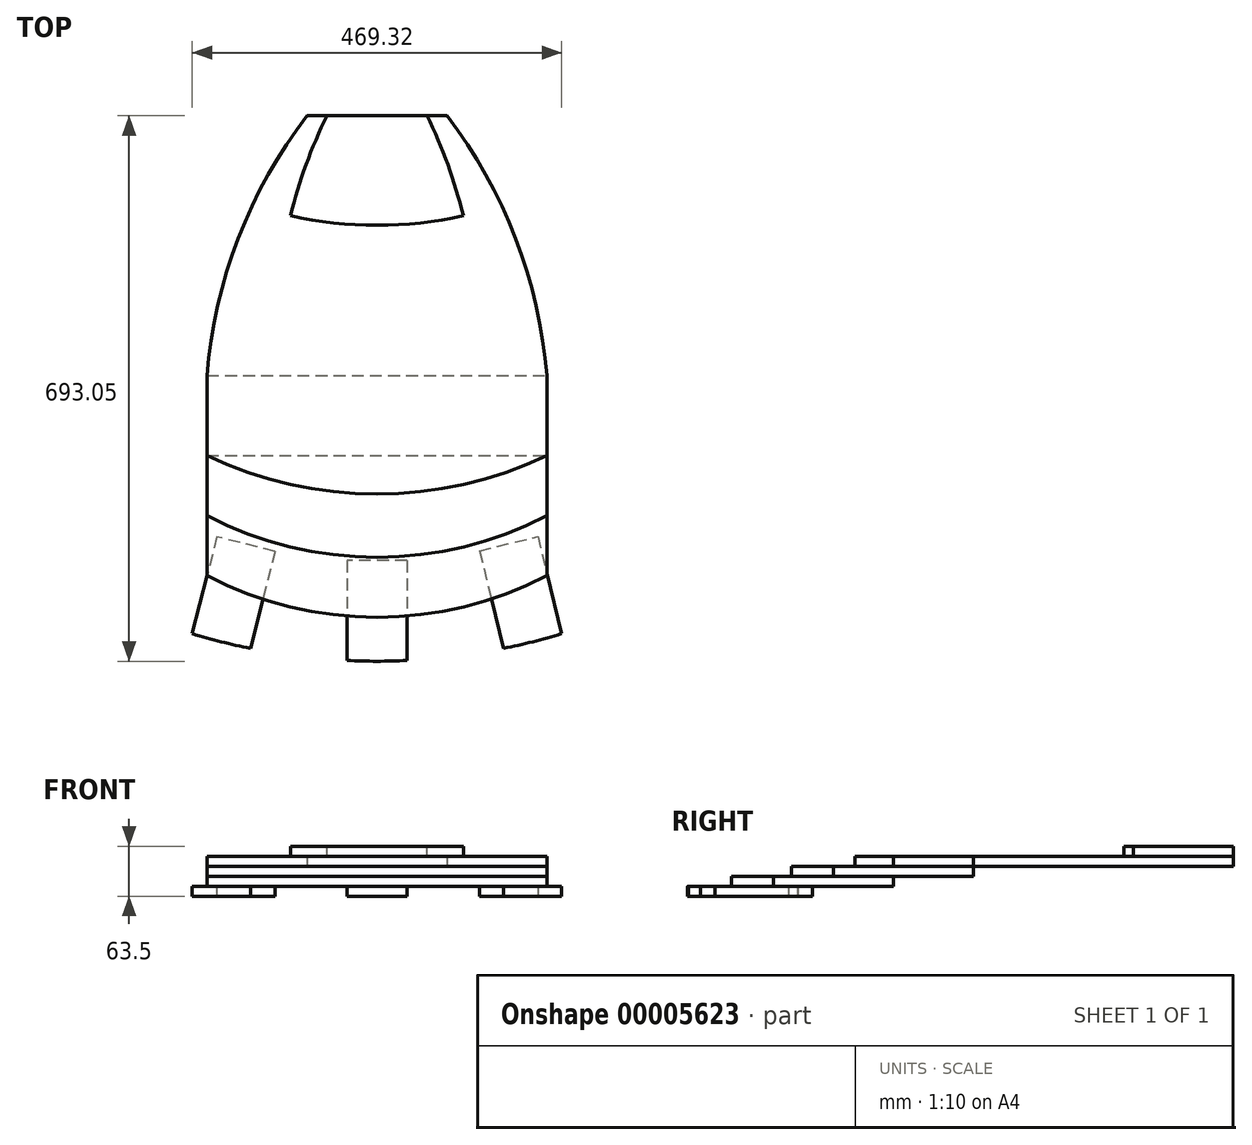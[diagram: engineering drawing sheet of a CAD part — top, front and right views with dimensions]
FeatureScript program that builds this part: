
annotation { "Feature Type Name" : "Feature", "Feature Type Description" : "" }
export const myFeature = defineFeature(function(context is Context, id is Id, definition is map)
    precondition{}
    {
        {
            var Q0;
            Q0=qCreatedBy(makeId("Top.planeOp"),FACE);
            cPlane(context, id + "F0", {"entities" : qUnion([Q0]), "cplaneType" : CPlaneType.OFFSET, "offset" : 25.4 * mm, "oppositeDirection" : true, "width" : 152.4 * mm, "height" : 152.4 * mm});
        }
        {
            var Q0;
            Q0=qCreatedBy(makeId("Top.planeOp"),FACE);
            cPlane(context, id + "F1", {"entities" : qUnion([Q0]), "cplaneType" : CPlaneType.OFFSET, "offset" : 38.1 * mm, "oppositeDirection" : true, "width" : 152.4 * mm, "height" : 152.4 * mm});
        }
        {
            var Q0;
            Q0=qCreatedBy(makeId("Top.planeOp"),FACE);
            cPlane(context, id + "F2", {"entities" : qUnion([Q0]), "cplaneType" : CPlaneType.OFFSET, "offset" : 50.8 * mm, "oppositeDirection" : true, "width" : 152.4 * mm, "height" : 152.4 * mm});
        }
        {
            var Q0;
            Q0=qCreatedBy(makeId("Top.planeOp"),FACE);
            cPlane(context, id + "F3", {"entities" : qUnion([Q0]), "cplaneType" : CPlaneType.OFFSET, "offset" : 63.5 * mm, "oppositeDirection" : true, "width" : 152.4 * mm, "height" : 152.4 * mm});
        }
        {
            var Q0;
            Q0=qCreatedBy(makeId("Top.planeOp"),FACE);
            var sketch = newSketch(context, id + "F4", { "sketchPlane" : qUnion([Q0])});
            skLineSegment(sketch, "E0.bottom", {"start": v(63.5, 0) * mm, "end": v(-63.5, 0) * mm});
            skArc(sketch, "E1.0.MirrorCS", {"start": v(-109.72, -127) * mm, "mid": v(-90.04, -62.25) * mm, "end": v(-63.5, 0) * mm});
            skArc(sketch, "E2.0.MirrorCS", {"start": v(109.72, -127) * mm, "mid": v(0, -139.15) * mm, "end": v(-109.72, -127) * mm});
            skArc(sketch, "E3.0.MirrorCS", {"start": v(63.5, 0) * mm, "mid": v(90.04, -62.25) * mm, "end": v(109.72, -127) * mm});
            skSolve(sketch);
        }
        {
            var Q0;
            Q0=makeQuery(id+"F4.imprint","IMPRINT",FACE,{"disambiguationData":[TD([[makeQuery(id+"F4.imprint","IMPRINT",EDGE,{"derivedFrom":sQuery(id+"F4.wireOp",EDGE,"E0.bottom")}),1.0]])]});
            extrude(context, id + "F5", {"entities" : qUnion([Q0]), "oppositeDirection" : true, "depth" : 12.7 * mm});
        }
        {
            var Q0;
            Q0=qCreatedBy(id+"F0.planeOp",FACE);
            var sketch = newSketch(context, id + "F6", { "sketchPlane" : qUnion([Q0])});
            skLineSegment(sketch, "E4", {"start": v(-88.9, 0) * mm, "end": v(88.9, 0) * mm});
            skArc(sketch, "E5", {"start": v(-215.9, -431.8) * mm, "mid": v(0, -480.67) * mm, "end": v(215.9, -431.8) * mm});
            skArc(sketch, "E6", {"start": v(-88.9, 0) * mm, "mid": v(-176.18, -155.96) * mm, "end": v(-215.9, -330.2) * mm});
            skArc(sketch, "E7", {"start": v(215.9, -330.2) * mm, "mid": v(176.18, -155.96) * mm, "end": v(88.9, 0) * mm});
            skLineSegment(sketch, "E8", {"start": v(-215.9, -431.8) * mm, "end": v(-215.9, -330.2) * mm});
            skLineSegment(sketch, "E9", {"start": v(215.9, -431.8) * mm, "end": v(215.9, -330.2) * mm});
            skSolve(sketch);
        }
        {
            var Q0;
            Q0=makeQuery(id+"F6.imprint","IMPRINT",FACE,{"disambiguationData":[TD([[makeQuery(id+"F6.imprint","IMPRINT",EDGE,{"derivedFrom":makeQuery(id+"F5.opExtrude","CAP_EDGE",EDGE,{"disambiguationData":[OSD([sQuery(id+"F4.wireOp",EDGE,"E0.top")])],"isStart":false})}),-1.0]])]});
            var Q1;
            Q1=makeQuery(id+"F6.imprint","IMPRINT",FACE,{"disambiguationData":[TD([[makeQuery(id+"F6.imprint","IMPRINT",EDGE,{"derivedFrom":sQuery(id+"F6.wireOp",EDGE,"E5")}),1.0]])]});
            var Q2;
            {var subQ1=makeQuery(id+"F5.opExtrude","CAP_EDGE",EDGE,{"disambiguationData":[OSD([sQuery(id+"F4.wireOp",EDGE,"8de56a55-3745-45d6-922e-69d785513ef6")])],"isStart":false});Q2=makeQuery(id+"F6.imprint","IMPRINT",FACE,{"disambiguationData":[TD([[makeQuery(id+"F6.imprint","IMPRINT",EDGE,{"derivedFrom":subQ1}),-1.0]])]});}
            extrude(context, id + "F7", {"entities" : qUnion([Q0, Q1, Q2]), "depth" : 12.7 * mm});
        }
        {
            var Q0;
            Q0=qCreatedBy(id+"F1.planeOp",FACE);
            var sketch = newSketch(context, id + "F8", { "sketchPlane" : qUnion([Q0])});
            skLineSegment(sketch, "E10", {"start": v(-215.9, -330.2) * mm, "end": v(215.9, -330.2) * mm});
            skLineSegment(sketch, "E11", {"start": v(215.9, -330.2) * mm, "end": v(215.9, -508) * mm});
            skLineSegment(sketch, "E12", {"start": v(-215.9, -508) * mm, "end": v(-215.9, -330.2) * mm});
            skArc(sketch, "E13", {"start": v(-215.9, -508) * mm, "mid": v(0, -561) * mm, "end": v(215.9, -508) * mm});
            skSolve(sketch);
        }
        {
            var Q0;
            {var subQ3=sQuery(id+"F8.wireOp",EDGE,"E10");Q0=makeQuery(id+"F8.imprint","IMPRINT",FACE,{"disambiguationData":[TD([[makeQuery(id+"F8.imprint","IMPRINT",EDGE,{"derivedFrom":subQ3}),-1.0]])]});}
            var Q1;
            {var subQ1=sQuery(id+"F8.wireOp",EDGE,"E13");Q1=makeQuery(id+"F8.imprint","IMPRINT",FACE,{"disambiguationData":[TD([[makeQuery(id+"F8.imprint","IMPRINT",EDGE,{"derivedFrom":subQ1}),1.0]])]});}
            extrude(context, id + "F9", {"entities" : qUnion([Q0, Q1]), "depth" : 12.7 * mm});
        }
        {
            var Q0;
            Q0=qCreatedBy(id+"F2.planeOp",FACE);
            var sketch = newSketch(context, id + "F10", { "sketchPlane" : qUnion([Q0])});
            skLineSegment(sketch, "E14", {"start": v(-215.9, -431.8) * mm, "end": v(215.9, -431.8) * mm});
            skLineSegment(sketch, "E15", {"start": v(215.9, -431.8) * mm, "end": v(215.9, -584.2) * mm});
            skLineSegment(sketch, "E16", {"start": v(-215.9, -584.2) * mm, "end": v(-215.9, -431.8) * mm});
            skArc(sketch, "E17", {"start": v(-215.9, -584.2) * mm, "mid": v(0, -637.2) * mm, "end": v(215.9, -584.2) * mm});
            skSolve(sketch);
        }
        {
            var Q0;
            {var subQ3=sQuery(id+"F10.wireOp",EDGE,"E14");Q0=makeQuery(id+"F10.imprint","IMPRINT",FACE,{"disambiguationData":[TD([[makeQuery(id+"F10.imprint","IMPRINT",EDGE,{"derivedFrom":subQ3}),-1.0]])]});}
            var Q1;
            {var subQ1=sQuery(id+"F10.wireOp",EDGE,"E17");Q1=makeQuery(id+"F10.imprint","IMPRINT",FACE,{"disambiguationData":[TD([[makeQuery(id+"F10.imprint","IMPRINT",EDGE,{"derivedFrom":subQ1}),1.0]])]});}
            extrude(context, id + "F11", {"entities" : qUnion([Q0, Q1]), "depth" : 12.7 * mm});
        }
        {
            var Q0;
            Q0=qCreatedBy(id+"F3.planeOp",FACE);
            var sketch = newSketch(context, id + "F12", { "sketchPlane" : qUnion([Q0])});
            skLineSegment(sketch, "E18.bottom", {"start": v(130.48, -552.79) * mm, "end": v(204.5, -534.69) * mm});
            skLineSegment(sketch, "E18.left", {"start": v(130.48, -552.79) * mm, "end": v(160.8, -676.81) * mm});
            skLineSegment(sketch, "E18.right", {"start": v(204.5, -534.69) * mm, "end": v(234.66, -658.06) * mm});
            skLineSegment(sketch, "E19.bottom", {"start": v(-129.54, -553.72) * mm, "end": v(-203.4, -534.96) * mm});
            skLineSegment(sketch, "E19.left", {"start": v(-129.54, -553.72) * mm, "end": v(-160.8, -676.81) * mm});
            skLineSegment(sketch, "E19.right", {"start": v(-203.4, -534.96) * mm, "end": v(-234.66, -658.06) * mm});
            skLineSegment(sketch, "E20.bottom", {"start": v(38.1, -565.15) * mm, "end": v(-38.1, -565.15) * mm});
            skLineSegment(sketch, "E20.left", {"start": v(38.1, -565.15) * mm, "end": v(38.1, -692.15) * mm});
            skLineSegment(sketch, "E20.right", {"start": v(-38.1, -565.15) * mm, "end": v(-38.1, -692.15) * mm});
            skArc(sketch, "E21", {"start": v(-234.66, -658.06) * mm, "mid": v(-197.95, -668.3) * mm, "end": v(-160.8, -676.81) * mm});
            skArc(sketch, "E22.trimOffspring", {"start": v(160.8, -676.81) * mm, "mid": v(197.95, -668.3) * mm, "end": v(234.66, -658.06) * mm});
            skArc(sketch, "E23.trimOffspring", {"start": v(-38.1, -692.15) * mm, "mid": v(0, -693.05) * mm, "end": v(38.1, -692.15) * mm});
            skSolve(sketch);
        }
        {
            var Q0;
            {var subQ5=sQuery(id+"F12.wireOp",EDGE,"E18.bottom");Q0=makeQuery(id+"F12.imprint","IMPRINT",FACE,{"disambiguationData":[TD([[makeQuery(id+"F12.imprint","IMPRINT",EDGE,{"derivedFrom":subQ5}),-1.0]])]});}
            var Q1;
            {var subQ7=sQuery(id+"F12.wireOp",EDGE,"E22.trimOffspring");Q1=makeQuery(id+"F12.imprint","IMPRINT",FACE,{"disambiguationData":[TD([[makeQuery(id+"F12.imprint","IMPRINT",EDGE,{"derivedFrom":subQ7}),1.0]])]});}
            extrude(context, id + "F13", {"entities" : qUnion([Q0, Q1]), "operationType" : NewBodyOperationType.ADD, "depth" : 12.7 * mm});
        }
        {
            var Q0;
            {var subQ5=sQuery(id+"F12.wireOp",EDGE,"E20.bottom");Q0=makeQuery(id+"F12.imprint","IMPRINT",FACE,{"disambiguationData":[TD([[makeQuery(id+"F12.imprint","IMPRINT",EDGE,{"derivedFrom":subQ5}),1.0]])]});}
            var Q1;
            {var subQ5=sQuery(id+"F12.wireOp",EDGE,"E23.trimOffspring");Q1=makeQuery(id+"F12.imprint","IMPRINT",FACE,{"disambiguationData":[TD([[makeQuery(id+"F12.imprint","IMPRINT",EDGE,{"derivedFrom":subQ5}),1.0]])]});}
            extrude(context, id + "F14", {"entities" : qUnion([Q0, Q1]), "operationType" : NewBodyOperationType.ADD, "depth" : 12.7 * mm});
        }
        {
            var Q0;
            {var subQ5=sQuery(id+"F12.wireOp",EDGE,"E19.bottom");Q0=makeQuery(id+"F12.imprint","IMPRINT",FACE,{"disambiguationData":[TD([[makeQuery(id+"F12.imprint","IMPRINT",EDGE,{"derivedFrom":subQ5}),1.0]])]});}
            var Q1;
            {var subQ5=sQuery(id+"F12.wireOp",EDGE,"E21");Q1=makeQuery(id+"F12.imprint","IMPRINT",FACE,{"disambiguationData":[TD([[makeQuery(id+"F12.imprint","IMPRINT",EDGE,{"derivedFrom":subQ5}),1.0]])]});}
            extrude(context, id + "F15", {"entities" : qUnion([Q0, Q1]), "operationType" : NewBodyOperationType.ADD, "depth" : 12.7 * mm});
        }
    });
